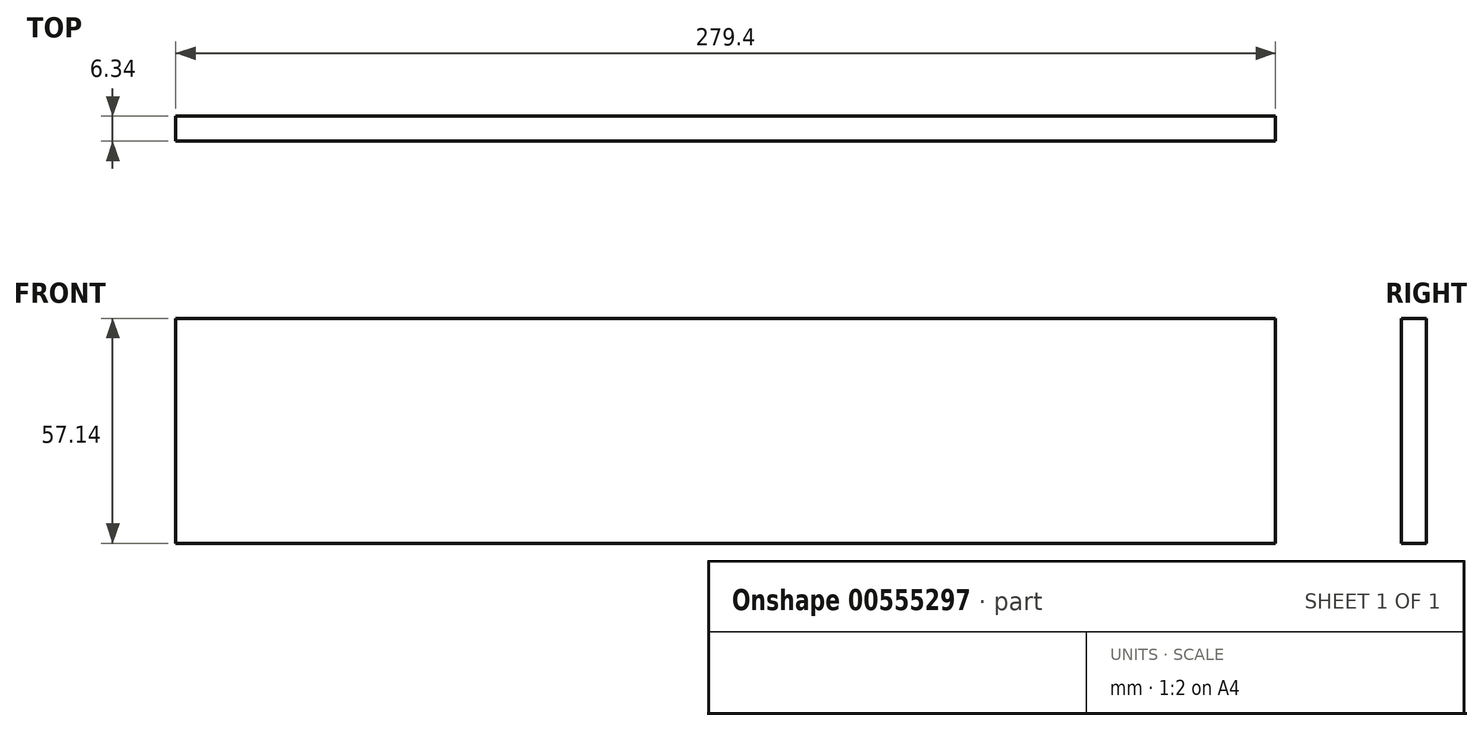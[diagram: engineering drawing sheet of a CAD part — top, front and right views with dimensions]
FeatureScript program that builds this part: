
annotation { "Feature Type Name" : "Feature", "Feature Type Description" : "" }
export const myFeature = defineFeature(function(context is Context, id is Id, definition is map)
    precondition{}
    {
        {
            var Q0;
            Q0=qCreatedBy(makeId("Front.planeOp"),FACE);
            var sketch = newSketch(context, id + "F0", { "sketchPlane" : qUnion([Q0])});
            skLineSegment(sketch, "E0.bottom", {"start": v(-139.7, 28.58) * mm, "end": v(139.7, 28.58) * mm});
            skLineSegment(sketch, "E0.top", {"start": v(-139.7, -28.58) * mm, "end": v(139.7, -28.58) * mm});
            skLineSegment(sketch, "E0.left", {"start": v(-139.7, 28.58) * mm, "end": v(-139.7, -28.58) * mm});
            skLineSegment(sketch, "E0.right", {"start": v(139.7, 28.58) * mm, "end": v(139.7, -28.58) * mm});
            skPoint(sketch, "E0.middle", {"position": v(0, 0) * mm});
            skSolve(sketch);
        }
        {
            var Q0;
            Q0=makeQuery(id+"F0.imprint","IMPRINT",FACE,{"disambiguationData":[TD([[makeQuery(id+"F0.imprint","IMPRINT",EDGE,{"derivedFrom":sQuery(id+"F0.wireOp",EDGE,"E0.bottom")}),-1.0]])]});
            extrude(context, id + "F1", {"entities" : qUnion([Q0]), "endBound" : BoundingType.SYMMETRIC, "depth" : 6.35 * mm, "offsetDistance" : 25.4 * mm});
        }
    });
